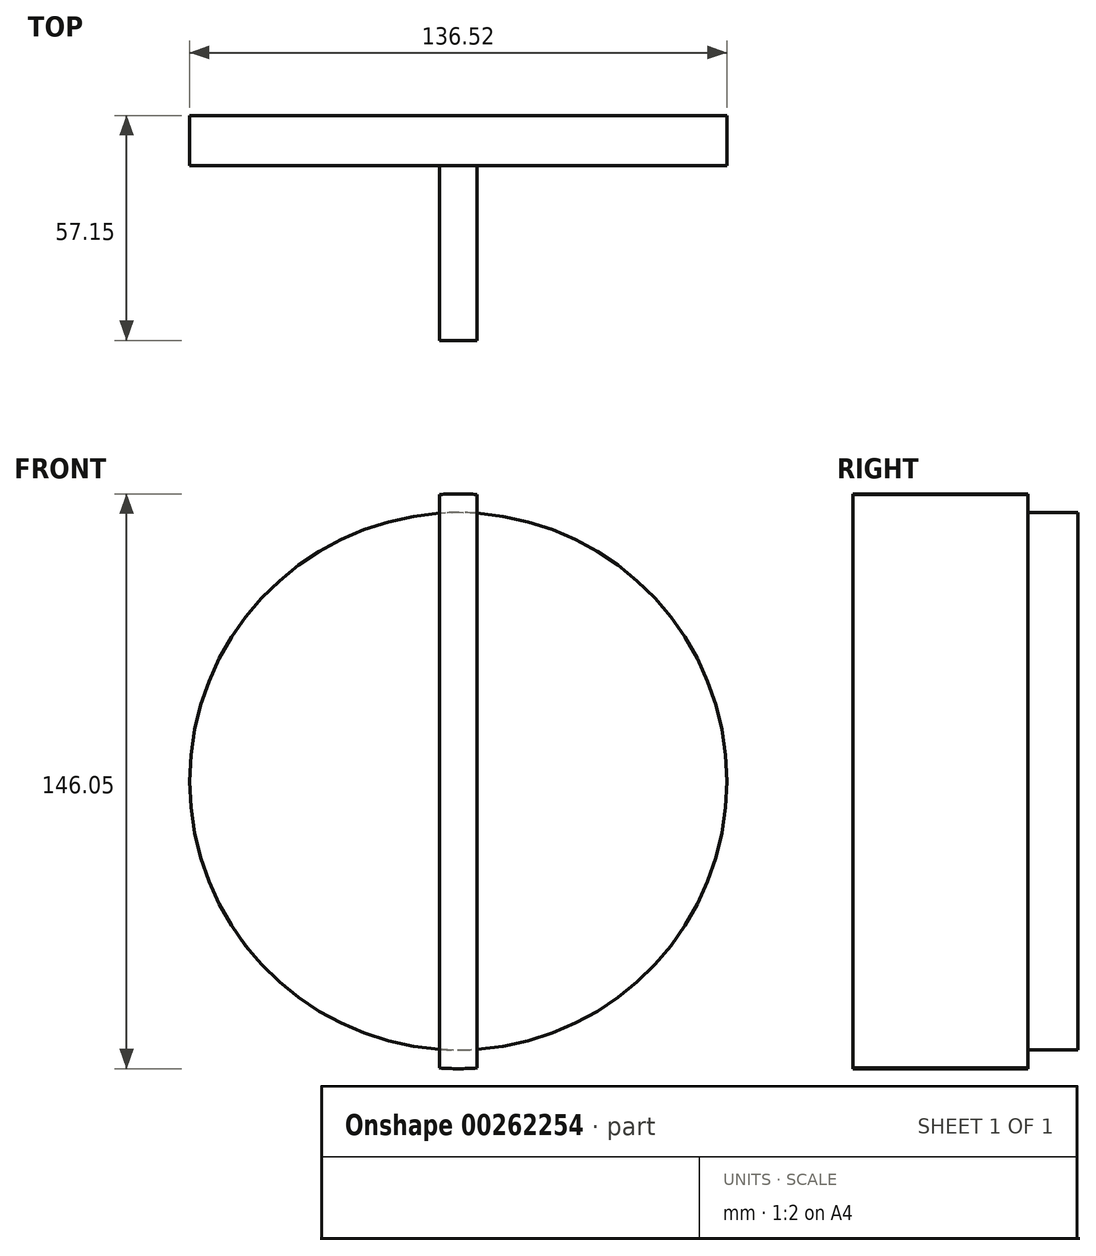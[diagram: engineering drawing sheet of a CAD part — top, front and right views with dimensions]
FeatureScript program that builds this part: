
annotation { "Feature Type Name" : "Feature", "Feature Type Description" : "" }
export const myFeature = defineFeature(function(context is Context, id is Id, definition is map)
    precondition{}
    {
        {
            var Q0;
            Q0=qCreatedBy(makeId("Front.planeOp"),FACE);
            var sketch = newSketch(context, id + "F0", { "sketchPlane" : qUnion([Q0])});
            skCircle(sketch, "E0", {"center": v(0, 0) * mm, "radius": 73.03 * mm});
            skLineSegment(sketch, "E1.bottom", {"start": v(4.76, 72.87) * mm, "end": v(-4.76, 72.87) * mm});
            skLineSegment(sketch, "E1.top", {"start": v(4.76, -72.87) * mm, "end": v(-4.76, -72.87) * mm});
            skLineSegment(sketch, "E1.left", {"start": v(4.76, 72.87) * mm, "end": v(4.76, -72.87) * mm});
            skLineSegment(sketch, "E1.right", {"start": v(-4.76, 72.87) * mm, "end": v(-4.76, -72.87) * mm});
            skLineSegment(sketch, "E2", {"start": v(73.03, 0) * mm, "end": v(55.2, 0) * mm});
            skCircle(sketch, "E3", {"center": v(55.2, 0) * mm, "radius": 6.35 * mm});
            skSolve(sketch);
        }
        {
            var Q0;
            Q0=qCreatedBy(makeId("Front.planeOp"),FACE);
            var sketch = newSketch(context, id + "F1", { "sketchPlane" : qUnion([Q0])});
            skCircle(sketch, "E4", {"center": v(0, 0) * mm, "radius": 68.26 * mm});
            skSolve(sketch);
        }
        {
            var Q0;
            {var subQ0=sQuery(id+"F0.wireOp",EDGE,"E1.bottom");Q0=makeQuery(id+"F0.imprint","IMPRINT",FACE,{"disambiguationData":[TD([[makeQuery(id+"F0.imprint","IMPRINT",EDGE,{"derivedFrom":subQ0}),-1.0]])]});}
            var Q1;
            {var subQ0=sQuery(id+"F0.wireOp",EDGE,"E1.top");Q1=makeQuery(id+"F0.imprint","IMPRINT",FACE,{"disambiguationData":[TD([[makeQuery(id+"F0.imprint","IMPRINT",EDGE,{"derivedFrom":subQ0}),1.0]])]});}
            var Q2;
            Q2=makeQuery(id+"F0.imprint","IMPRINT",FACE,{"disambiguationData":[TD([[makeQuery(id+"F0.imprint","IMPRINT",EDGE,{"derivedFrom":sQuery(id+"F0.wireOp",EDGE,"E1.bottom")}),1.0]])]});
            extrude(context, id + "F2", {"entities" : qUnion([Q0, Q1, Q2]), "depth" : 44.45 * mm});
        }
        {
            var Q0;
            Q0=makeQuery(id+"F1.imprint","IMPRINT",FACE,{"disambiguationData":[TD([[makeQuery(id+"F1.imprint","IMPRINT",EDGE,{"derivedFrom":sQuery(id+"F1.wireOp",EDGE,"E4")}),1.0]])]});
            extrude(context, id + "F3", {"entities" : qUnion([Q0]), "operationType" : NewBodyOperationType.ADD, "oppositeDirection" : true, "depth" : 12.7 * mm});
        }
    });
